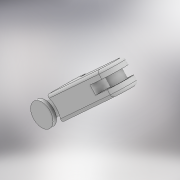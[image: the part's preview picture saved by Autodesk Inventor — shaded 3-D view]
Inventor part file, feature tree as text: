
AUTODESK INVENTOR PART (.ipt)
format: ipt  version: 2022 (Build 260153000, 153)  size: 181,248 bytes
history: native  units: mm
features: sketch x6, other x3
ambient origin geometry x8: Origin, YZ Plane, XZ Plane, XY Plane, X Axis, Y Axis, Z Axis, Center Point
bodies: Solid1 (feature_tree)
feature tree (9):
  other  "Upper Arm.ipt"
  other  "Solid1::Upper Arm.ipt"
  other  "TaggingFeature1"
  sketch  "Sketch1"  dims[d0=10.0mm]
  sketch  "Sketch2"
  sketch  "Sketch3"
  sketch  "Sketch4"
  sketch  "Sketch5"
  sketch  "Sketch6"
